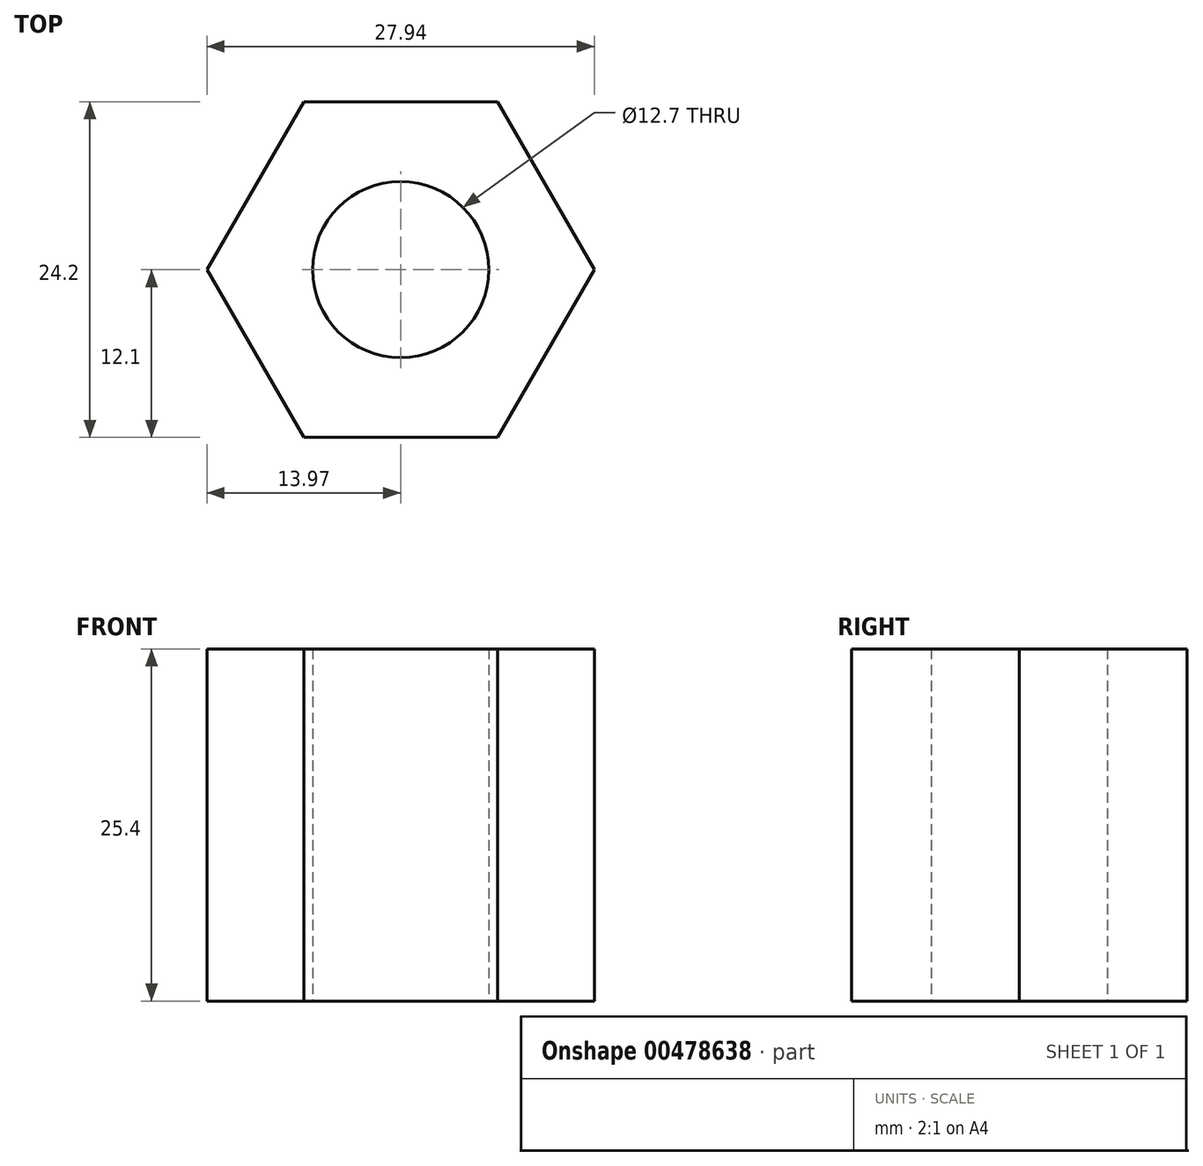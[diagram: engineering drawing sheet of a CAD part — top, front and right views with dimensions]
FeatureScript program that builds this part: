
annotation { "Feature Type Name" : "Feature", "Feature Type Description" : "" }
export const myFeature = defineFeature(function(context is Context, id is Id, definition is map)
    precondition{}
    {
        {
            var Q0;
            Q0=qCreatedBy(makeId("Top.planeOp"),FACE);
            var sketch = newSketch(context, id + "F0", { "sketchPlane" : qUnion([Q0])});
            skCircle(sketch, "E0.cCircle", {"center": v(0, 0) * mm, "radius": 12.1 * mm, "construction": true});
            skLineSegment(sketch, "E0.0", {"start": v(-6.98, 12.1) * mm, "end": v(6.98, 12.1) * mm});
            skLineSegment(sketch, "E0.1", {"start": v(6.99, 12.1) * mm, "end": v(13.97, 0) * mm});
            skLineSegment(sketch, "E0.2", {"start": v(13.97, 0) * mm, "end": v(6.99, -12.1) * mm});
            skLineSegment(sketch, "E0.3", {"start": v(6.99, -12.1) * mm, "end": v(-6.98, -12.1) * mm});
            skLineSegment(sketch, "E0.4", {"start": v(-6.98, -12.1) * mm, "end": v(-13.97, 0) * mm});
            skLineSegment(sketch, "E0.5", {"start": v(-13.97, 0) * mm, "end": v(-6.99, 12.1) * mm});
            skPoint(sketch, "E0.0.midPoint", {"position": v(0, 12.1) * mm});
            skCircle(sketch, "E1", {"center": v(0, 0) * mm, "radius": 6.35 * mm});
            skSolve(sketch);
        }
        {
            var Q0;
            Q0 = qSketchRegion(id + "F0", true);
            var Q1;
            Q1=makeQuery(id+"F0.imprint","IMPRINT",FACE,{"disambiguationData":[TD([[makeQuery(id+"F0.imprint","IMPRINT",EDGE,{"derivedFrom":sQuery(id+"F0.wireOp",EDGE,"E0.0")}),-1.0]])]});
            extrude(context, id + "F1", {"entities" : qUnion([Q0, Q1]), "depth" : 25.4 * mm, "offsetDistance" : 25.4 * mm});
        }
    });
